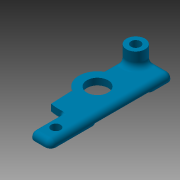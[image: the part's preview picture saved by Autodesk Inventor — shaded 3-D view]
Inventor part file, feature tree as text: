
AUTODESK INVENTOR PART (.ipt)
format: ipt  version: 2014 (Build 180170000, 170)  size: 121,856 bytes
history: native  units: mm
features: other x3, extrude x1, projected_geometry x1
ambient origin geometry x8: Origin, YZ Plane, XZ Plane, XY Plane, X Axis, Y Axis, Z Axis, Center Point
bodies: Solid1 (feature_tree)
feature tree (5):
  other  "bowden-extruder.ipt"
  extrude  "Extrusion1"  Depth=10.0mm
  other  "tensioner top::bowden-extruder.ipt"
  other  "TaggingFeature1"
  projected_geometry  "Projected Loop1"
